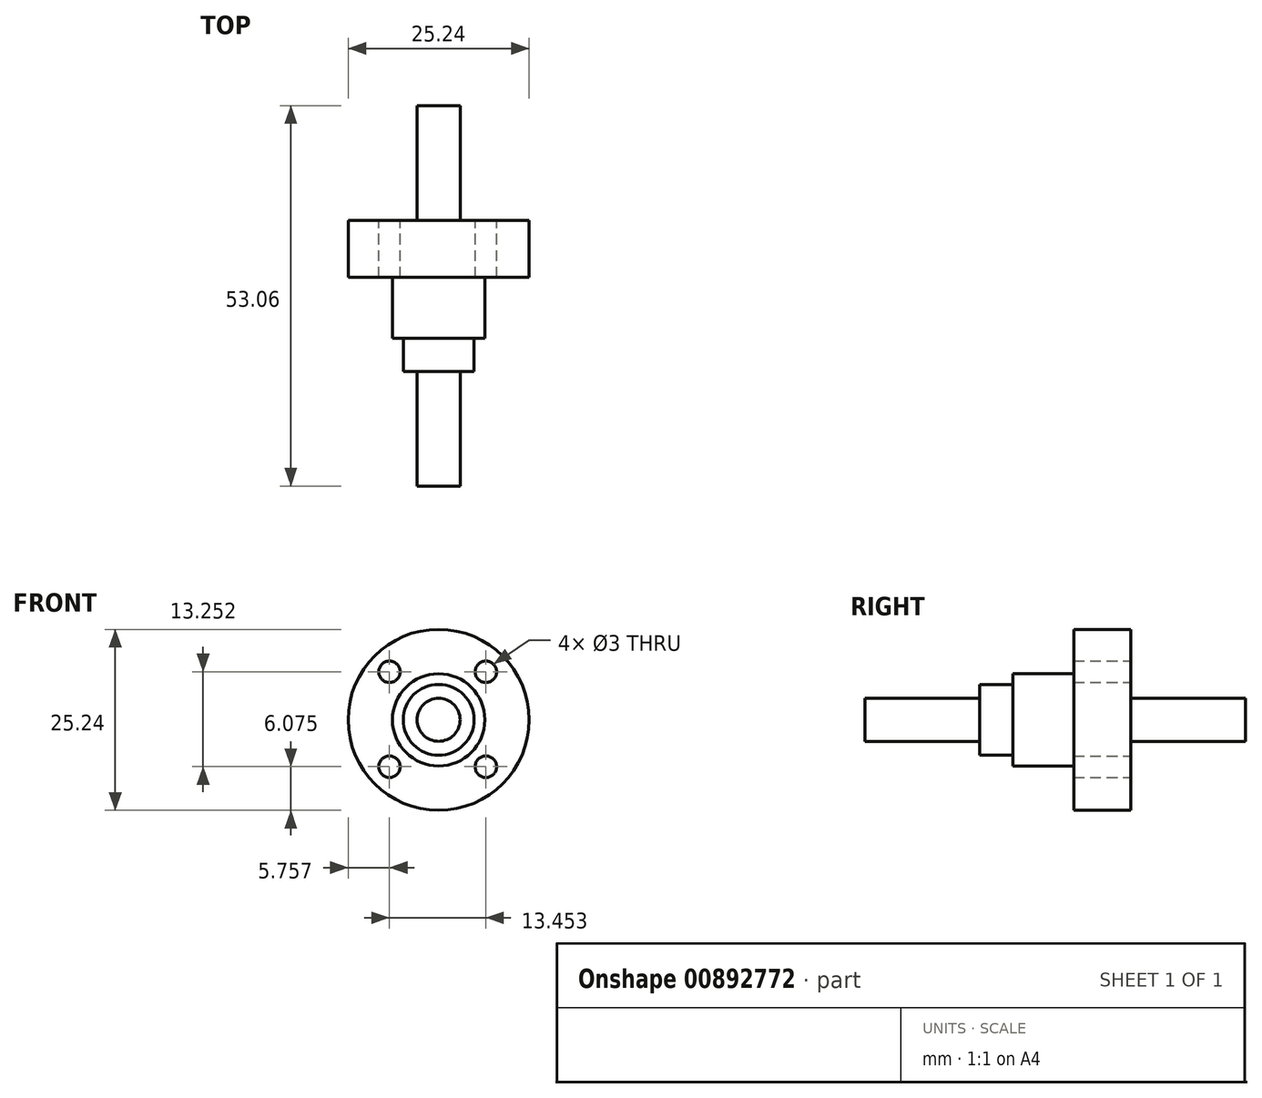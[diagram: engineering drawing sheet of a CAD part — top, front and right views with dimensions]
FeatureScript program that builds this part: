
annotation { "Feature Type Name" : "Feature", "Feature Type Description" : "" }
export const myFeature = defineFeature(function(context is Context, id is Id, definition is map)
    precondition{}
    {
        {
            var Q0;
            Q0=qCreatedBy(makeId("Front.planeOp"),FACE);
            var sketch = newSketch(context, id + "F0", { "sketchPlane" : qUnion([Q0])});
            skCircle(sketch, "E0", {"center": v(0, 0) * mm, "radius": 3 * mm});
            skSolve(sketch);
        }
        {
            var Q0;
            Q0=qCreatedBy(makeId("Front.planeOp"),FACE);
            var sketch = newSketch(context, id + "F1", { "sketchPlane" : qUnion([Q0])});
            skCircle(sketch, "E1", {"center": v(0, 0) * mm, "radius": 4.94 * mm});
            skSolve(sketch);
        }
        {
            var Q0;
            Q0=qCreatedBy(makeId("Front.planeOp"),FACE);
            var sketch = newSketch(context, id + "F2", { "sketchPlane" : qUnion([Q0])});
            skCircle(sketch, "E2", {"center": v(0, 0) * mm, "radius": 6.44 * mm});
            skSolve(sketch);
        }
        {
            var Q0;
            Q0=qCreatedBy(makeId("Front.planeOp"),FACE);
            var sketch = newSketch(context, id + "F3", { "sketchPlane" : qUnion([Q0])});
            skCircle(sketch, "E3", {"center": v(0, 0) * mm, "radius": 12.62 * mm});
            skSolve(sketch);
        }
        {
            var Q0;
            Q0=qCreatedBy(makeId("Front.planeOp"),FACE);
            var sketch = newSketch(context, id + "F4", { "sketchPlane" : qUnion([Q0])});
            skCircle(sketch, "E4", {"center": v(-6.86, 6.7) * mm, "radius": 0.5 * mm});
            skCircle(sketch, "E5", {"center": v(6.6, 6.7) * mm, "radius": 0.5 * mm});
            skCircle(sketch, "E6", {"center": v(6.6, -6.55) * mm, "radius": 0.5 * mm});
            skCircle(sketch, "E7", {"center": v(-6.86, -6.55) * mm, "radius": 0.5 * mm});
            skSolve(sketch);
        }
        {
            var Q0;
            Q0 = qSketchRegion(id + "F0", true);
            extrude(context, id + "F5", {"entities" : qUnion([Q0]), "depth" : 37.08 * mm, "offsetDistance" : 25.4 * mm, "hasSecondDirection" : true, "secondDirectionOppositeDirection" : true, "secondDirectionDepth" : 15.98 * mm});
        }
        {
            var Q0;
            Q0 = qSketchRegion(id + "F1", true);
            extrude(context, id + "F6", {"entities" : qUnion([Q0]), "operationType" : NewBodyOperationType.ADD, "depth" : 21.08 * mm, "offsetDistance" : 25.4 * mm});
        }
        {
            var Q0;
            Q0 = qSketchRegion(id + "F2", true);
            extrude(context, id + "F7", {"entities" : qUnion([Q0]), "operationType" : NewBodyOperationType.ADD, "depth" : 16.48 * mm, "offsetDistance" : 25.4 * mm});
        }
        {
            var Q0;
            Q0 = qSketchRegion(id + "F3", true);
            extrude(context, id + "F8", {"entities" : qUnion([Q0]), "operationType" : NewBodyOperationType.ADD, "depth" : 7.98 * mm, "offsetDistance" : 25.4 * mm});
        }
        {
            var Q0;
            Q0=sQuery(id+"F4.wireOp",VERTEX,"E4.center");
            var Q1;
            Q1=sQuery(id+"F4.wireOp",VERTEX,"E5.center");
            var Q2;
            Q2=sQuery(id+"F4.wireOp",VERTEX,"E6.center");
            var Q3;
            Q3=sQuery(id+"F4.wireOp",VERTEX,"E7.center");
            var Q4;
            Q4=makeQuery(id+"F5.opExtrude","SWEPT_BODY",BODY,{"disambiguationData":[OSD([sQuery(id+"F0.wireOp",EDGE,"E0")])]});
            hole(context, id + "F9", {"style" : HoleStyle.SIMPLE, "endStyle" : HoleEndStyle.THROUGH, "oppositeDirection" : true, "holeDiameter" : 3 * mm, "majorDiameter" : 6.35 * mm, "isTappedThrough" : true, "tappedDepth" : 12.7 * mm, "tapClearance" : 3, "locations" : qUnion([Q0, Q1, Q2, Q3]), "scope" : qUnion([Q4])});
        }
    });
